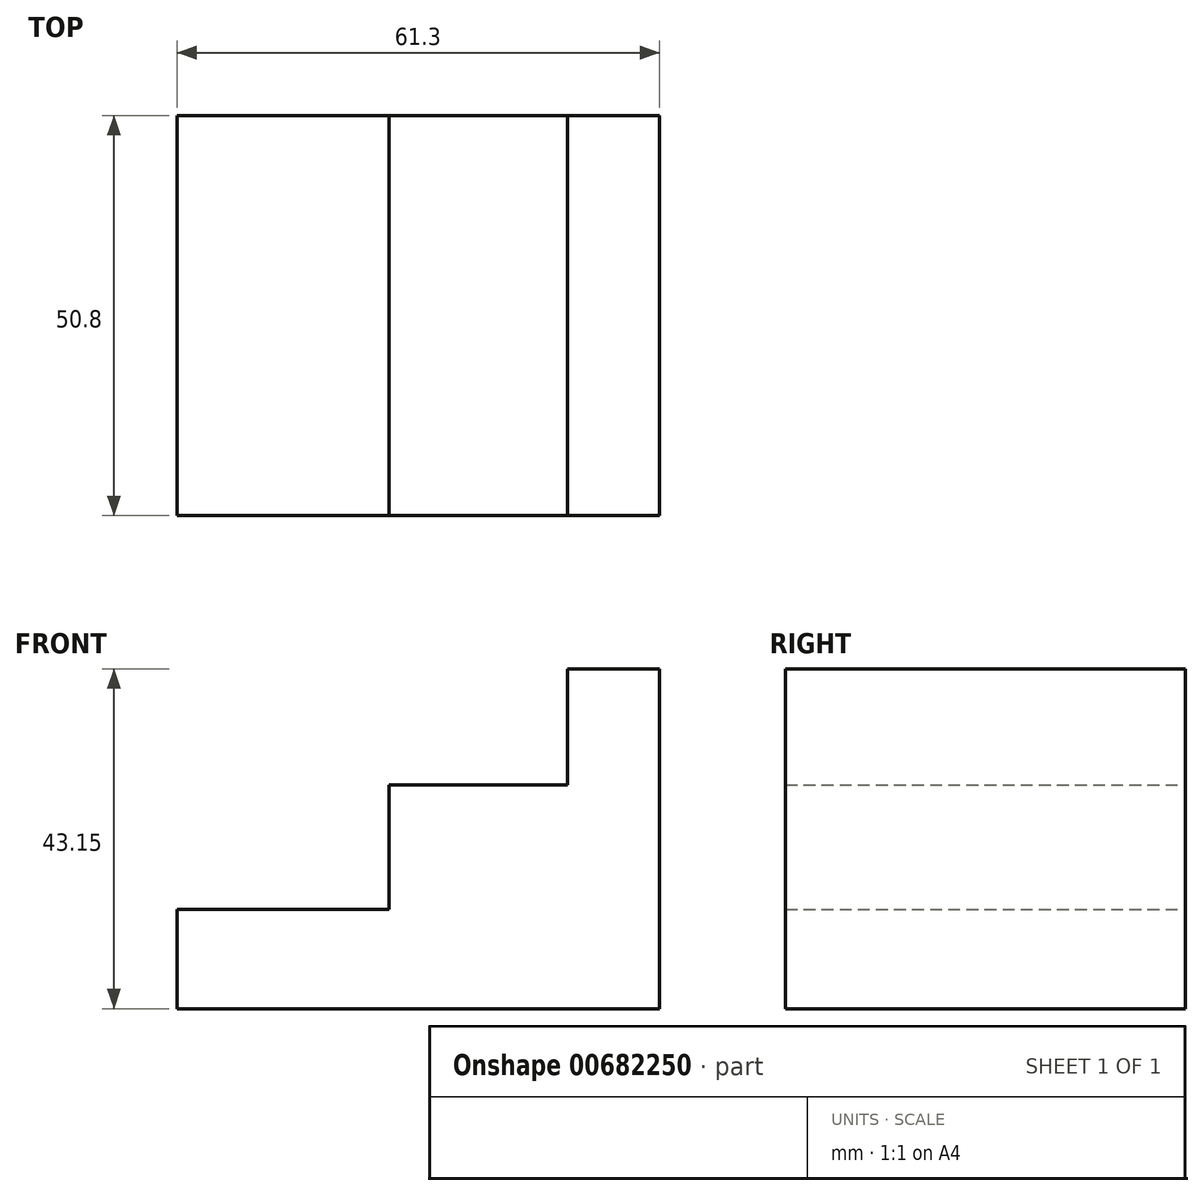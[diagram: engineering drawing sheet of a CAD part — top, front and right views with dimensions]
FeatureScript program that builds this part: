
annotation { "Feature Type Name" : "Feature", "Feature Type Description" : "" }
export const myFeature = defineFeature(function(context is Context, id is Id, definition is map)
    precondition{}
    {
        {
            var Q0;
            Q0=qCreatedBy(makeId("Front.planeOp"),FACE);
            var sketch = newSketch(context, id + "F0", { "sketchPlane" : qUnion([Q0])});
            skLineSegment(sketch, "E0", {"start": v(-72.09, 10.22) * mm, "end": v(-9.45, 10.22) * mm});
            skLineSegment(sketch, "E1", {"start": v(-9.45, 10.22) * mm, "end": v(-9.45, 53.37) * mm});
            skLineSegment(sketch, "E2", {"start": v(-9.45, 53.37) * mm, "end": v(-21.1, 53.37) * mm});
            skLineSegment(sketch, "E3", {"start": v(-21.1, 53.37) * mm, "end": v(-21.1, 38.67) * mm});
            skLineSegment(sketch, "E4", {"start": v(-21.1, 38.67) * mm, "end": v(-43.82, 38.67) * mm});
            skLineSegment(sketch, "E5", {"start": v(-43.82, 38.67) * mm, "end": v(-43.82, 22.82) * mm});
            skLineSegment(sketch, "E6", {"start": v(-43.82, 22.82) * mm, "end": v(-70.75, 22.82) * mm});
            skLineSegment(sketch, "E7", {"start": v(-70.75, 22.82) * mm, "end": v(-70.75, 10.22) * mm});
            skSolve(sketch);
        }
        {
            var Q0;
            Q0 = qSketchRegion(id + "F0", true);
            extrude(context, id + "F1", {"entities" : qUnion([Q0]), "depth" : 50.8 * mm, "offsetDistance" : 25.4 * mm});
        }
    });
